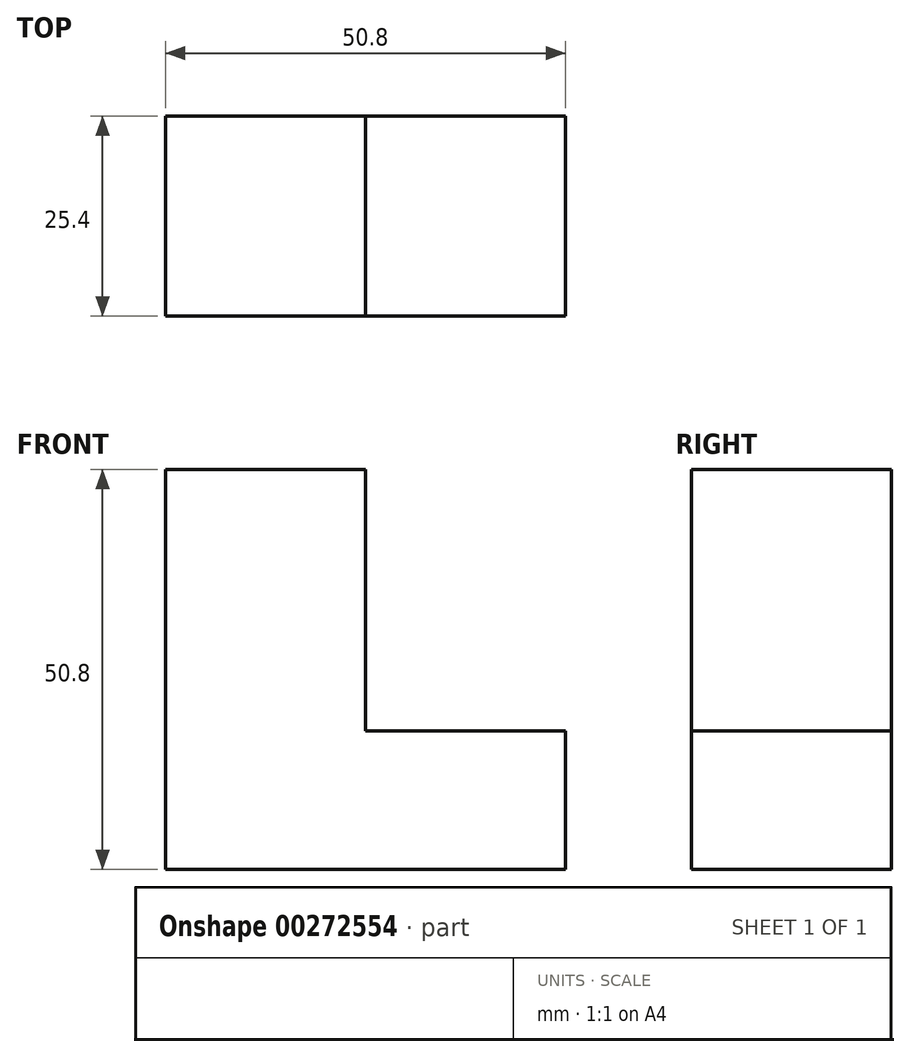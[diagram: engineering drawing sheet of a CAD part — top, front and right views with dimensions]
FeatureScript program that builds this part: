
annotation { "Feature Type Name" : "Feature", "Feature Type Description" : "" }
export const myFeature = defineFeature(function(context is Context, id is Id, definition is map)
    precondition{}
    {
        {
            var Q0;
            Q0=qCreatedBy(makeId("Front.planeOp"),FACE);
            var sketch = newSketch(context, id + "F0", { "sketchPlane" : qUnion([Q0])});
            skLineSegment(sketch, "E0", {"start": v(0, 0) * mm, "end": v(-50.8, 0) * mm});
            skLineSegment(sketch, "E1", {"start": v(-50.8, 0) * mm, "end": v(-50.8, 50.8) * mm});
            skLineSegment(sketch, "E2", {"start": v(-50.8, 50.8) * mm, "end": v(-25.4, 50.8) * mm});
            skLineSegment(sketch, "E3", {"start": v(-25.4, 50.8) * mm, "end": v(-25.4, 17.59) * mm});
            skLineSegment(sketch, "E4", {"start": v(-25.4, 17.59) * mm, "end": v(0, 17.59) * mm});
            skLineSegment(sketch, "E5", {"start": v(0, 17.59) * mm, "end": v(0, 0) * mm});
            skSolve(sketch);
        }
        {
            var Q0;
            Q0 = qSketchRegion(id + "F0", true);
            extrude(context, id + "F1", {"entities" : qUnion([Q0]), "depth" : 25.4 * mm});
        }
    });
